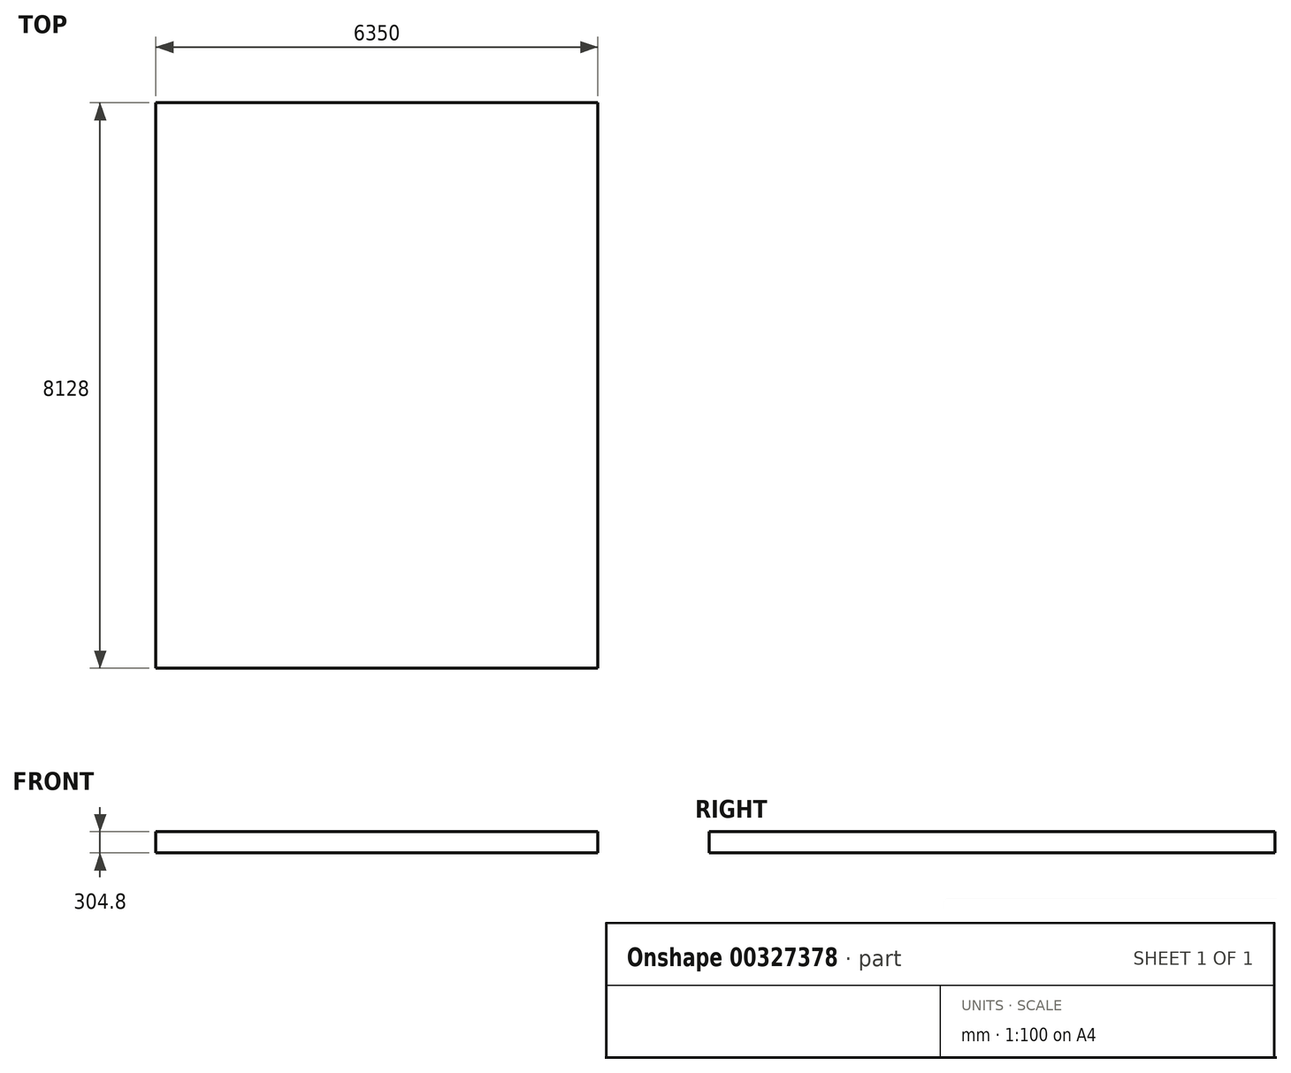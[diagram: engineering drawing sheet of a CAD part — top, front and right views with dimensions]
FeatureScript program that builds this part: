
annotation { "Feature Type Name" : "Feature", "Feature Type Description" : "" }
export const myFeature = defineFeature(function(context is Context, id is Id, definition is map)
    precondition{}
    {
        {
            var Q0;
            Q0=qCreatedBy(makeId("Top.planeOp"),FACE);
            var sketch = newSketch(context, id + "F0", { "sketchPlane" : qUnion([Q0])});
            skLineSegment(sketch, "E0.bottom", {"start": v(0, 0) * mm, "end": v(6350, 0) * mm});
            skLineSegment(sketch, "E0.top", {"start": v(0, 8128) * mm, "end": v(6350, 8128) * mm});
            skLineSegment(sketch, "E0.left", {"start": v(0, 0) * mm, "end": v(0, 8128) * mm});
            skLineSegment(sketch, "E0.right", {"start": v(6350, 0) * mm, "end": v(6350, 8128) * mm});
            skSolve(sketch);
        }
        {
            var Q0;
            Q0=makeQuery(id+"F0.imprint","IMPRINT",FACE,{"disambiguationData":[TD([[makeQuery(id+"F0.imprint","IMPRINT",EDGE,{"derivedFrom":sQuery(id+"F0.wireOp",EDGE,"E0.bottom")}),1.0]])]});
            extrude(context, id + "F1", {"entities" : qUnion([Q0]), "oppositeDirection" : true, "depth" : 304.8 * mm});
        }
    });
